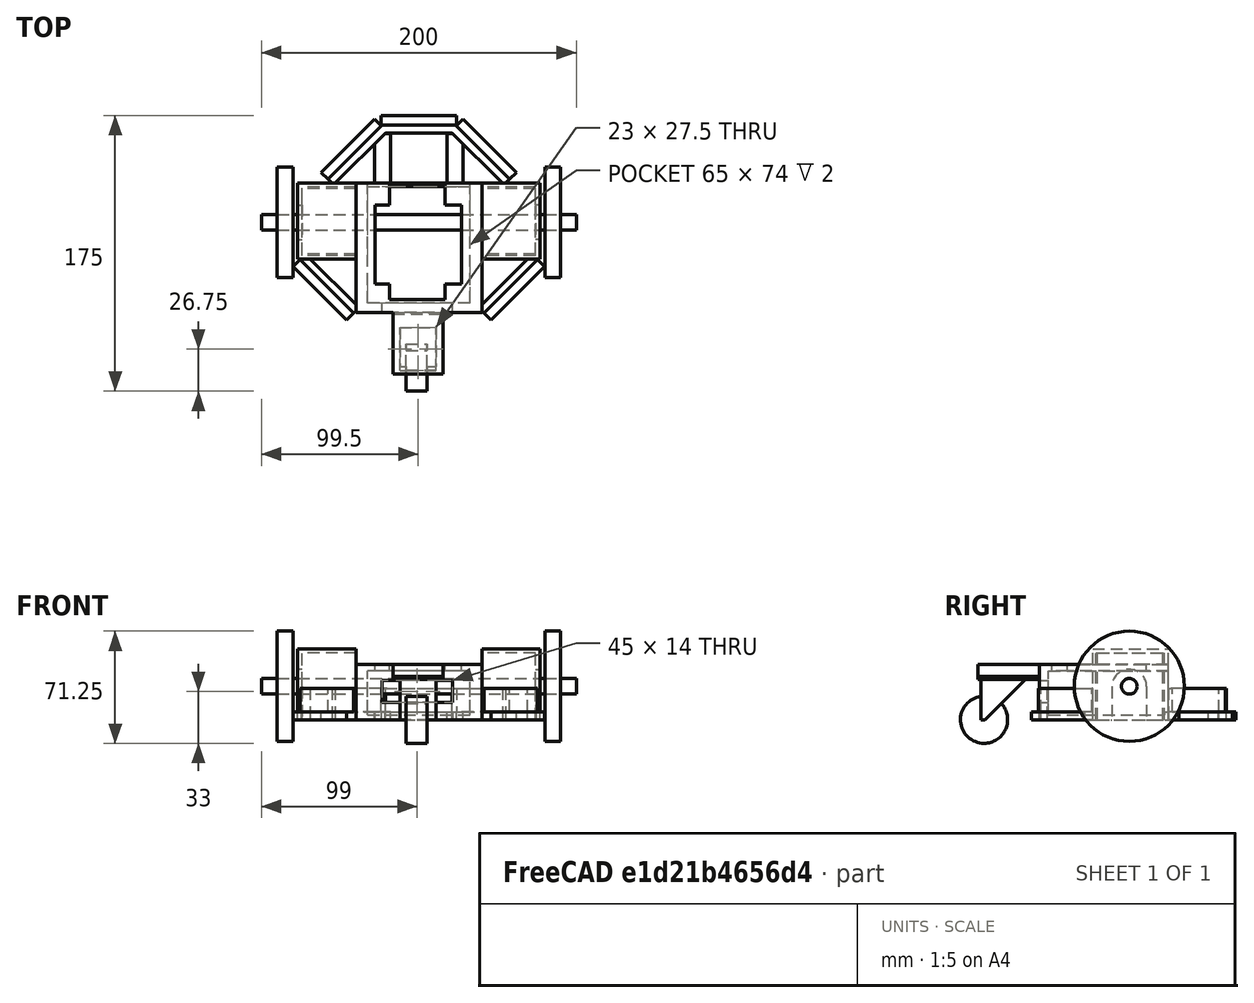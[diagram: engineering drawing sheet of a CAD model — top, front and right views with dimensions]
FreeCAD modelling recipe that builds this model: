
FCSTD DOCUMENT  (FreeCAD 0.19R)
Label: Rootbot-0v1-proto
License: All rights reserved
LicenseURL: http://en.wikipedia.org/wiki/All_rights_reserved
objects: Part::Box×21, Part::MultiFuse×14, App::DocumentObjectGroup×6, Part::Cut×6, Part::Cylinder×5, Part::Mirroring×5, Part::Chamfer×1, Part::FeaturePython×1, Part::Compound×1
note: 54 computed .brp shape members not serialized (recipe doc carries the construction recipe); baked Part::Feature solids carry a one-line shape summary decoded from their .brp

FEATURE [Part::Box] Box001  label="Chassis"
  AttacherType = Attacher::AttachEngine3D
  Height = 45
  Length = 80
  Placement = pos=(0,-6,0) rot=(0,0,1;0rad)
  Width = 82
FEATURE [Part::Box] Box002  label="StepperMountL"
  AttacherType = Attacher::AttachEngine3D
  Height = 42.5
  Length = 42.5
  Placement = pos=(0,30,0) rot=(0,0,1;1.5708rad)
  Width = 34
FEATURE [Part::Box] Box003  label="StepperMountR"
  AttacherType = Attacher::AttachEngine3D
  Height = 42.5
  Length = 42.5
  Placement = pos=(114,30,0) rot=(0,0,1;1.5708rad)
  Width = 34
FEATURE [Part::Cylinder] Cylinder  label="StepperAxis"
  Angle = 360
  AttacherType = Attacher::AttachEngine3D
  Height = 200
  Placement = pos=(-60,51.25,21.25) rot=(0,1,0;1.5708rad)
  Radius = 5
FEATURE [App::DocumentObjectGroup] Group003  label="Stepper"
  Group = -> [Box002,Box003,Cylinder]
FEATURE [Part::Cylinder] Cylinder001  label="WheelL"
  Angle = 360
  AttacherType = Attacher::AttachEngine3D
  Height = 10
  Placement = pos=(-50,51.25,21.25) rot=(0,1,0;1.5708rad)
  Radius = 35
FEATURE [Part::Cylinder] Cylinder002  label="WheelR"
  Angle = 360
  AttacherType = Attacher::AttachEngine3D
  Height = 10
  Placement = pos=(120,51.25,21.25) rot=(0,1,0;1.5708rad)
  Radius = 35
FEATURE [Part::Cylinder] Cylinder003  label="SwivelWheel"
  Angle = 360
  AttacherType = Attacher::AttachEngine3D
  Height = 13.25
  Placement = pos=(4,-148,0) rot=(0,1,0;1.5708rad)
  Radius = 15
FEATURE [Part::Box] Box004  label="Cube"
  AttacherType = Attacher::AttachEngine3D
  Height = 27.5
  Length = 23
  Placement = pos=(0,-150,0) rot=(0,0,1;0rad)
  Width = 27.5
FEATURE [Part::Chamfer] Chamfer
  Base = -> Box004
  Edges = 1 edges r=25: [Edge11]
FEATURE [Part::Box] Box005  label="BasePlate"
  AttacherType = Attacher::AttachEngine3D
  Height = 2
  Length = 32
  Placement = pos=(-4.5,-152,25.5) rot=(0,0,1;0rad)
  Width = 38
FEATURE [Part::MultiFuse] Fusion  label="SwivelFusion"
  Placement = pos=(28,107,0) rot=(0,0,1;0rad)
  Shapes = -> [Cylinder003,Box005,Chamfer]
FEATURE [App::DocumentObjectGroup] Group005  label="Swivel"
  Group = -> [Fusion]
FEATURE [App::DocumentObjectGroup] Group004  label="Wheels"
  Group = -> [Cylinder002,Cylinder001,Group005]
FEATURE [App::DocumentObjectGroup] Group002  label="BatteryCompound"
FEATURE [App::DocumentObjectGroup] Group  label="Components"
  Group = -> [Group002,Group003,Group004]
FEATURE [Part::Box] Box  label="MotorCaseR"
  AttacherType = Attacher::AttachEngine3D
  Height = 45
  Length = 37
  Placement = pos=(-37,28,0) rot=(0,0,1;0rad)
  Width = 48
FEATURE [Part::Mirroring] Part__Mirroring  label="MotorCaseL"
  Base = (0,0,0)
  Normal = (1,0,0)
  Placement = pos=(80,0,0) rot=(0,0,1;0rad)
  Source = -> Box
FEATURE [Part::MultiFuse] Fusion001
  Shapes = -> [Part__Mirroring,Box,Box001]
FEATURE [Part::Box] Box006  label="SwivelHolder"
  AttacherType = Attacher::AttachEngine3D
  Height = 10
  Length = 32
  Placement = pos=(23.5,-45,27.5) rot=(0,0,1;0rad)
  Width = 39
FEATURE [Part::MultiFuse] Fusion002
  Shapes = -> [Box006,Fusion001]
FEATURE [Part::Box] Box007  label="StepperMountR001"
  AttacherType = Attacher::AttachEngine3D
  Height = 42.5
  Length = 42.5
  Placement = pos=(114,30,0) rot=(0,0,1;1.5708rad)
  Width = 34
FEATURE [Part::Box] Box008  label="StepperMountL001"
  AttacherType = Attacher::AttachEngine3D
  Height = 42.5
  Length = 42.5
  Placement = pos=(0,30,0) rot=(0,0,1;1.5708rad)
  Width = 34
FEATURE [Part::MultiFuse] Fusion003  label="MotorPlaceholder"
  Placement = pos=(0,1,0) rot=(0,0,1;0rad)
  Shapes = -> [Box008,Box007]
FEATURE [Part::Cut] Cut
  Base = -> Fusion002
  Tool = -> Fusion003
FEATURE [Part::Cylinder] Cylinder004  label="Cylinder"
  Angle = 360
  AttacherType = Attacher::AttachEngine3D
  Height = 3
  Placement = pos=(114,51.25,21) rot=(0,1,0;1.5708rad)
  Radius = 11
FEATURE [Part::Box] Box009  label="Cube001"
  AttacherType = Attacher::AttachEngine3D
  Height = 21
  Length = 3
  Placement = pos=(117,40.25,21) rot=(0,1,0;3.14159rad)
  Width = 22
FEATURE [Part::MultiFuse] Fusion004  label="StepperAxisMotorHousingHoleL"
  Shapes = -> [Cylinder004,Box009]
FEATURE [Part::Mirroring] Part__Mirroring001  label="StepperAxisMotorHousingHoleL (Mirror #2)"
  Base = (0,0,0)
  Normal = (1,0,0)
  Placement = pos=(80,0,0) rot=(0,0,1;0rad)
  Source = -> Fusion004
FEATURE [Part::MultiFuse] Fusion005
  Shapes = -> [Part__Mirroring001,Fusion004]
FEATURE [Part::Cut] Cut001
  Base = -> Cut
  Tool = -> Fusion005
FEATURE [Part::Box] Box010  label="Battery"
  AttacherType = Attacher::AttachEngine3D
  Height = 28
  Length = 76
  Placement = pos=(72.5,0,3) rot=(0,0,1;1.5708rad)
  Width = 65
FEATURE [Part::Cut] Cut002
  Base = -> Cut001
  Tool = -> Box010
FEATURE [Part::Box] Box011  label="Cube002"
  AttacherType = Attacher::AttachEngine3D
  Height = 2
  Length = 65
  Placement = pos=(7.5,74,3) rot=(0,0,1;0rad)
  Width = 2
FEATURE [Part::MultiFuse] Fusion006
  Shapes = -> [Box011,Cut002]
FEATURE [Part::Box] Box012  label="Cube003"
  AttacherType = Attacher::AttachEngine3D
  Height = 10
  Length = 121
  Placement = pos=(80,-45,35) rot=(0,0,1;1.5708rad)
  Width = 80
FEATURE [Part::Box] Box013  label="Cube004"
  AttacherType = Attacher::AttachEngine3D
  Height = 10
  Length = 50
  Placement = pos=(67.25,12,29) rot=(0,0,1;1.5708rad)
  Width = 55
FEATURE [Part::Cut] Cut003
  Base = -> Fusion006
  Tool = -> Box012
FEATURE [Part::Box] Box014  label="Cube005"
  AttacherType = Attacher::AttachEngine3D
  Height = 10
  Length = 74
  Placement = pos=(56.5,2,29) rot=(0,0,1;1.5708rad)
  Width = 35
FEATURE [Part::MultiFuse] Fusion007
  Shapes = -> [Box013,Box014]
FEATURE [Part::Cut] Cut004
  Base = -> Cut003
  Tool = -> Fusion007
FEATURE [Part::Box] Box015  label="Cube006"
  AttacherType = Attacher::AttachEngine3D
  Height = 14
  Length = 6
  Placement = pos=(61.5,-6,11) rot=(0,0,1;1.5708rad)
  Width = 45
FEATURE [Part::Cut] Cut005
  Base = -> Cut004
  Refine = true
  Tool = -> Box015
FEATURE [Part::Box] Box016  label="Cube007"
  AttacherType = Attacher::AttachEngine3D
  Height = 5
  Length = 48
  Placement = pos=(60.25,109,0) rot=(0,0,-1;0.785398rad)
  Width = 11
FEATURE [Part::Box] Box017  label="Cube008"
  AttacherType = Attacher::AttachEngine3D
  Height = 20
  Length = 48
  Placement = pos=(60.25,109,0) rot=(0,0,-1;0.785398rad)
  Width = 5
FEATURE [Part::MultiFuse] Fusion008  label="SonarFR"
  Shapes = -> [Box016,Box017]
FEATURE [Part::Mirroring] Part__Mirroring002  label="SonarFL"
  Base = (0,0,0)
  Normal = (1,0,0)
  Placement = pos=(80,0,0) rot=(0,0,1;0rad)
  Source = -> Fusion008
FEATURE [Part::Mirroring] Part__Mirroring003  label="SonarRRCopy"
  Base = (0,0,0)
  Normal = (0,1,0)
  Placement = pos=(17.75,106,0) rot=(0,0,-1;0rad)
  Source = -> Fusion008
FEATURE [Part::Box] Box018  label="Cube009"
  AttacherType = Attacher::AttachEngine3D
  Height = 5
  Length = 32
  Placement = pos=(58,107.5,0) rot=(0,0,-1;1.5708rad)
  Width = 10
FEATURE [Part::MultiFuse] Fusion009  label="SonarRR"
  Shapes = -> [Box018,Part__Mirroring003]
FEATURE [Part::Mirroring] Part__Mirroring004  label="SonarRL"
  Base = (0,0,0)
  Normal = (1,0,0)
  Placement = pos=(80,0,0) rot=(0,0,1;0rad)
  Source = -> Fusion009
FEATURE [Part::MultiFuse] Fusion010
  Shapes = -> [Fusion009,Part__Mirroring004]
FEATURE [Part::MultiFuse] Fusion011
  Shapes = -> [Part__Mirroring002,Fusion008]
FEATURE [Part::FeaturePython] Connect  # WARN: FeaturePython — macro-defined, semantics opaque (R4)
  Objects = -> [Fusion010,Cut005]
  Tolerance = 0
FEATURE [Part::MultiFuse] Fusion012  label="Rootbot001"
  Shapes = -> [Connect,Fusion011]
FEATURE [Part::Box] Box019  label="Cube010"
  AttacherType = Attacher::AttachEngine3D
  Height = 5
  Length = 48
  Placement = pos=(16,108,0) rot=(0,0,-1;0rad)
  Width = 11
FEATURE [Part::Box] Box020  label="Cube011"
  AttacherType = Attacher::AttachEngine3D
  Height = 20
  Length = 48
  Placement = pos=(16,108,0) rot=(0,0,-1;0rad)
  Width = 5
FEATURE [Part::MultiFuse] Fusion013  label="Rootbot002"
  Shapes = -> [Fusion012,Box019,Box020]
FEATURE [App::DocumentObjectGroup] Group001  label="Rootbot"
  Group = -> [Cut005,Fusion013]
FEATURE [Part::Compound] Compound
  Links = -> [Fusion013]
